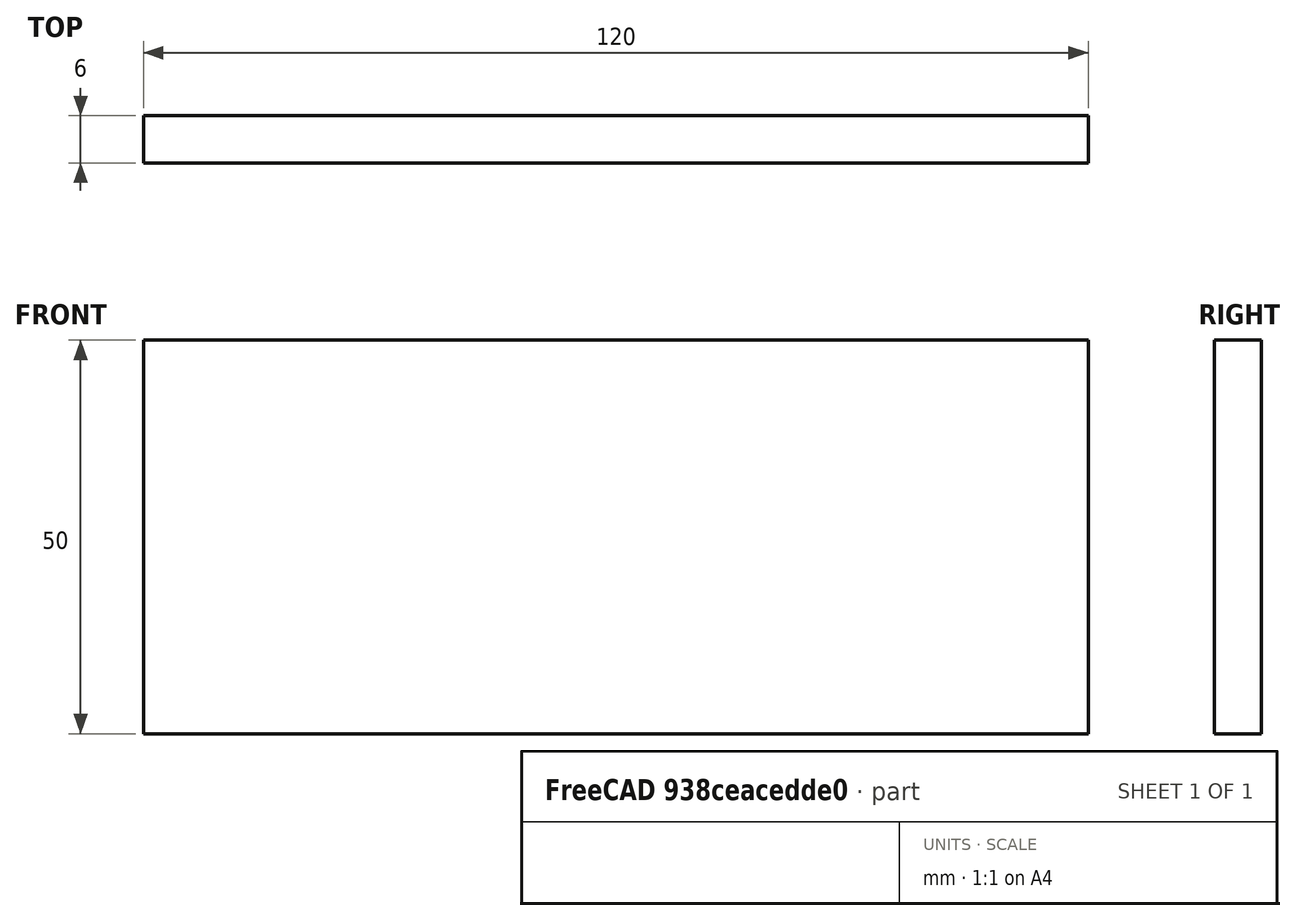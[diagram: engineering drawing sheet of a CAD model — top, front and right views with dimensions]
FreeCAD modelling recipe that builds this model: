
FCSTD DOCUMENT  (FreeCAD 0.15R4671 (Git))
Label: Flat Bar 120x6 EN10058 S235JR
License: All rights reserved
LicenseURL: http://en.wikipedia.org/wiki/All_rights_reserved
objects: Sketcher::SketchObject×1, Part::Extrusion×1
note: 2 computed .brp shape members not serialized (recipe doc carries the construction recipe); baked Part::Feature solids carry a one-line shape summary decoded from their .brp

FEATURE [Sketcher::SketchObject] Sketch
  sketch-geometry (4):
    g0: LineSegment StartX=-60 StartY=-3 StartZ=0 EndX=60 EndY=-3 EndZ=0
    g1: LineSegment StartX=60 StartY=-3 StartZ=0 EndX=60 EndY=3 EndZ=0
    g2: LineSegment StartX=60 StartY=3 StartZ=0 EndX=-60 EndY=3 EndZ=0
    g3: LineSegment StartX=-60 StartY=3 StartZ=0 EndX=-60 EndY=-3 EndZ=0
  constraints (12):
    c: Coincident(g0,g1)
    c: Coincident(g1,g2)
    c: Coincident(g2,g3)
    c: Coincident(g3,g0)
    c: Horizontal(g0)
    c: Horizontal(g2)
    c: Vertical(g1)
    c: Vertical(g3)
    c: Symmetric(g1,g2,g-2)
    c: Symmetric(g0,g1,g-1)
    c: DistanceY(g1) = 6
    c: DistanceX(g0) = 120
FEATURE [Part::Extrusion] Extrude  label="Flat Bar 120x6 EN10058 S235JR"
  Base = -> Sketch
  Dir = (0,0,50)
  Solid = true
